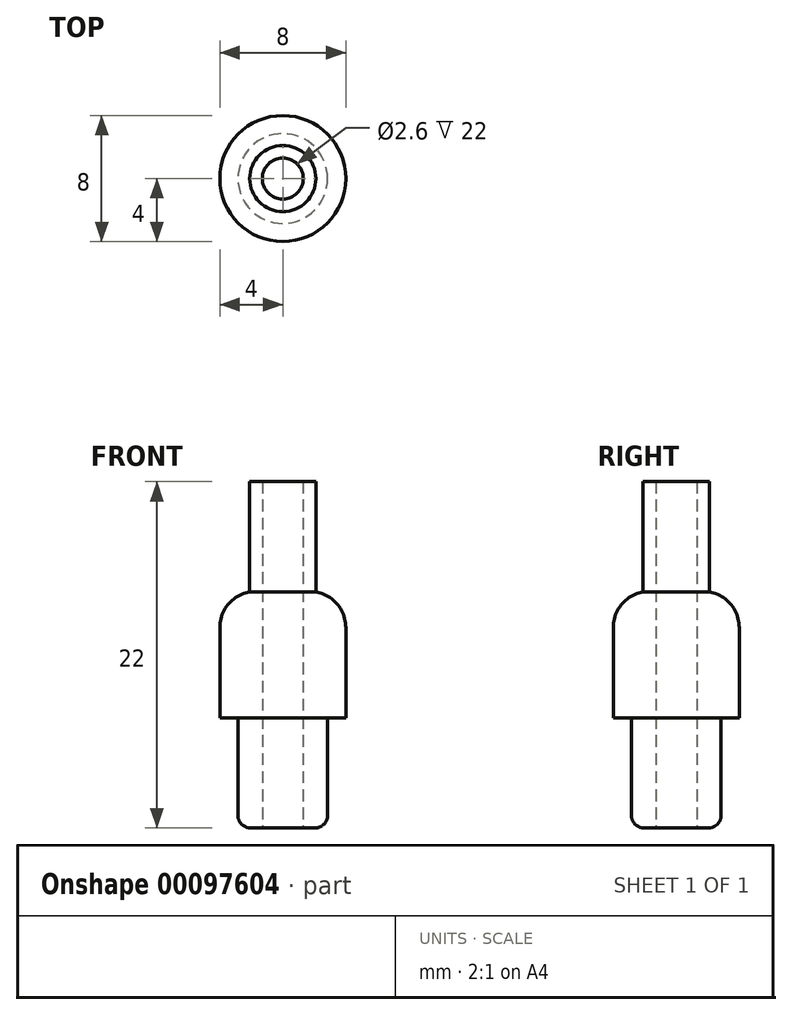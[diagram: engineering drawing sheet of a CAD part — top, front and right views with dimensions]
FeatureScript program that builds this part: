
annotation { "Feature Type Name" : "Feature", "Feature Type Description" : "" }
export const myFeature = defineFeature(function(context is Context, id is Id, definition is map)
    precondition{}
    {
        {
            var Q0;
            Q0=qCreatedBy(makeId("Top.planeOp"),FACE);
            var sketch = newSketch(context, id + "F0", { "sketchPlane" : qUnion([Q0])});
            skCircle(sketch, "E0", {"center": v(0, 0) * mm, "radius": 4 * mm});
            skCircle(sketch, "E1", {"center": v(0, 0) * mm, "radius": 2.1 * mm});
            skCircle(sketch, "E2", {"center": v(0, 0) * mm, "radius": 2.85 * mm});
            skCircle(sketch, "E3", {"center": v(0, 0) * mm, "radius": 1.3 * mm});
            skSolve(sketch);
        }
        {
            var Q0;
            Q0=makeQuery(id+"F0.imprint","IMPRINT",FACE,{"disambiguationData":[TD([[makeQuery(id+"F0.imprint","IMPRINT",EDGE,{"derivedFrom":sQuery(id+"F0.wireOp",EDGE,"E1")}),1.0]])]});
            var Q1;
            Q1=sQuery(id+"F0.wireOp",EDGE,"E1");
            var Q2;
            Q2=sQuery(id+"F0.wireOp",EDGE,"E2");
            extrude(context, id + "F1", {"entities" : qUnion([Q0]), "surfaceEntities" : qUnion([Q1, Q2]), "depth" : 15 * mm});
        }
        {
            var Q0;
            Q0=makeQuery(id+"F0.imprint","IMPRINT",FACE,{"disambiguationData":[TD([[makeQuery(id+"F0.imprint","IMPRINT",EDGE,{"derivedFrom":sQuery(id+"F0.wireOp",EDGE,"E1")}),1.0]])]});
            var Q1;
            Q1=makeQuery(id+"F0.imprint","IMPRINT",FACE,{"disambiguationData":[TD([[makeQuery(id+"F0.imprint","IMPRINT",EDGE,{"derivedFrom":sQuery(id+"F0.wireOp",EDGE,"E1")}),-1.0]])]});
            extrude(context, id + "F2", {"entities" : qUnion([Q0, Q1]), "operationType" : NewBodyOperationType.ADD, "oppositeDirection" : true, "depth" : 7 * mm});
        }
        {
            var Q0;
            Q0=makeQuery(id+"F0.imprint","IMPRINT",FACE,{"disambiguationData":[TD([[makeQuery(id+"F0.imprint","IMPRINT",EDGE,{"derivedFrom":sQuery(id+"F0.wireOp",EDGE,"E0")}),1.0]])]});
            var Q1;
            Q1=makeQuery(id+"F0.imprint","IMPRINT",FACE,{"disambiguationData":[TD([[makeQuery(id+"F0.imprint","IMPRINT",EDGE,{"derivedFrom":sQuery(id+"F0.wireOp",EDGE,"E1")}),-1.0]])]});
            extrude(context, id + "F3", {"entities" : qUnion([Q0, Q1]), "operationType" : NewBodyOperationType.ADD, "depth" : 8 * mm});
        }
        {
            var Q0;
            Q0=makeQuery(id+"F3.opExtrude","CAP_EDGE",EDGE,{"disambiguationData":[OSD([sQuery(id+"F0.wireOp",EDGE,"E0")])],"isStart":false});
            fillet(context, id + "F4", {"entities" : qUnion([Q0]), "radius" : 2.3 * mm, "allowEdgeOverflow" : false});
        }
        {
            var Q0;
            Q0=makeQuery(id+"F2.opExtrude","CAP_EDGE",EDGE,{"disambiguationData":[OSD([sQuery(id+"F0.wireOp",EDGE,"E2")])],"isStart":false});
            fillet(context, id + "F5", {"entities" : qUnion([Q0]), "radius" : 0.8 * mm, "tangentPropagation" : true, "allowEdgeOverflow" : false});
        }
    });
